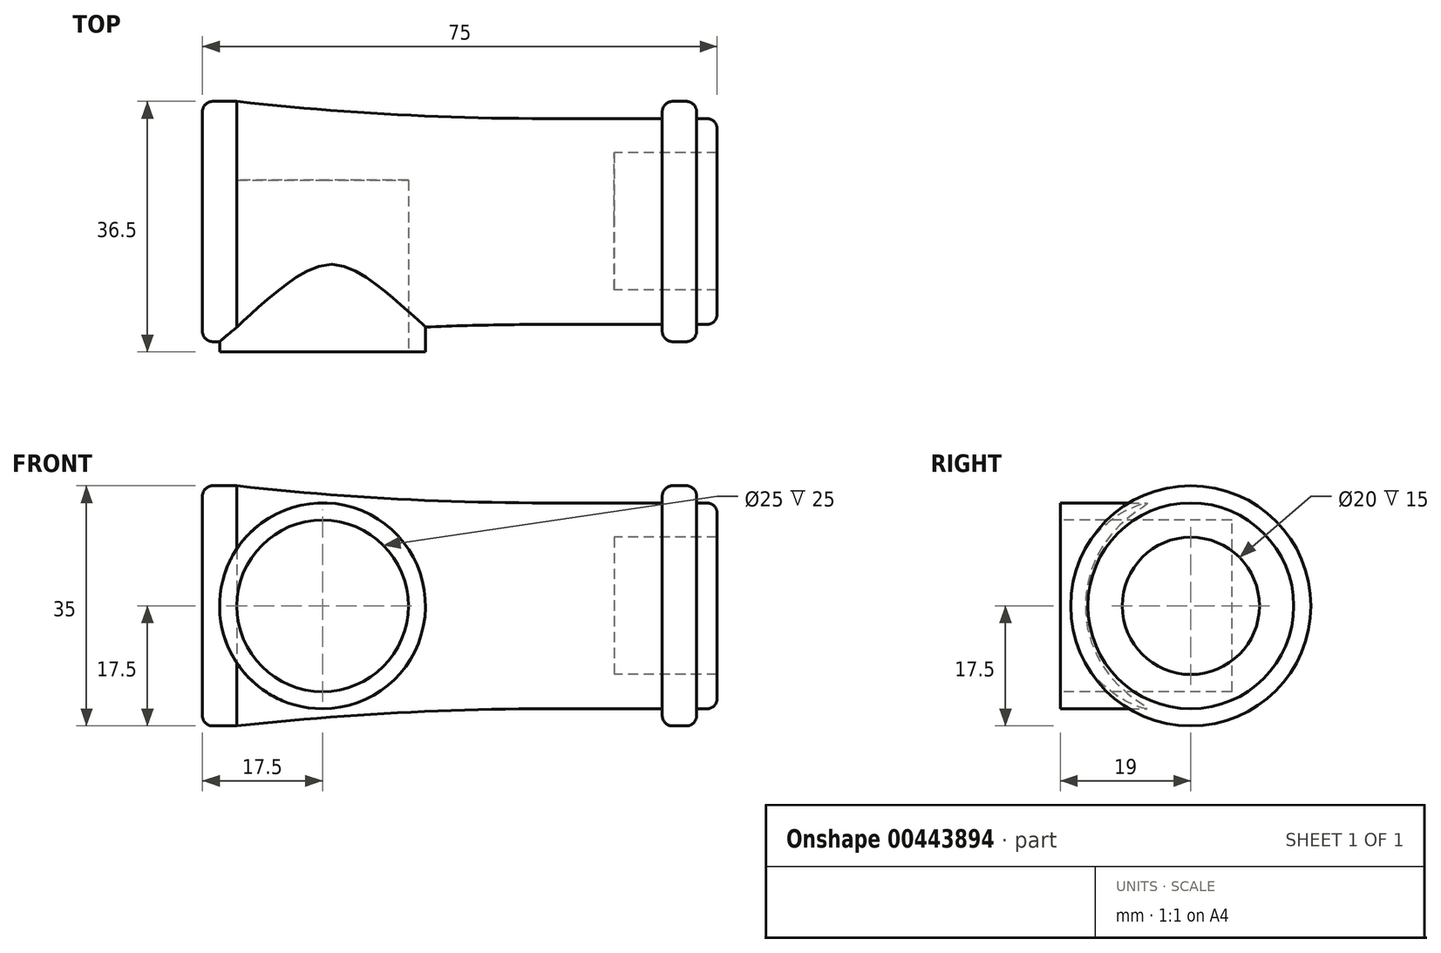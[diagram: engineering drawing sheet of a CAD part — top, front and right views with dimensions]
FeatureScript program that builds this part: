
annotation { "Feature Type Name" : "Feature", "Feature Type Description" : "" }
export const myFeature = defineFeature(function(context is Context, id is Id, definition is map)
    precondition{}
    {
        {
            var Q0;
            Q0=qCreatedBy(makeId("Front.planeOp"),FACE);
            var sketch = newSketch(context, id + "F0", { "sketchPlane" : qUnion([Q0])});
            skLineSegment(sketch, "E0", {"start": v(0, 0) * mm, "end": v(0, 17.5) * mm});
            skLineSegment(sketch, "E1", {"start": v(0, 17.5) * mm, "end": v(5, 17.5) * mm});
            skLineSegment(sketch, "E2", {"start": v(0, 0) * mm, "end": v(60, 0) * mm});
            skLineSegment(sketch, "E3", {"start": v(60, 0) * mm, "end": v(60, 10) * mm});
            skLineSegment(sketch, "E4", {"start": v(60, 10) * mm, "end": v(75, 10) * mm});
            skLineSegment(sketch, "E5", {"start": v(75, 10) * mm, "end": v(75, 15) * mm});
            skLineSegment(sketch, "E6", {"start": v(75, 15) * mm, "end": v(72, 15) * mm});
            skLineSegment(sketch, "E7", {"start": v(72, 15) * mm, "end": v(72, 17.5) * mm});
            skLineSegment(sketch, "E8", {"start": v(72, 17.5) * mm, "end": v(67, 17.5) * mm});
            skLineSegment(sketch, "E9", {"start": v(67, 17.5) * mm, "end": v(67, 15) * mm});
            skLineSegment(sketch, "E10", {"start": v(67, 15) * mm, "end": v(50, 15) * mm});
            skArc(sketch, "E11", {"start": v(5, 17.5) * mm, "mid": v(27.47, 15.63) * mm, "end": v(50, 15) * mm});
            skSolve(sketch);
        }
        {
            var Q0;
            Q0 = qSketchRegion(id + "F0", true);
            var Q1;
            Q1=sQuery(id+"F0.wireOp",EDGE,"E2");
            revolve(context, id + "F1", {"entities" : qUnion([Q0]), "axis" : qUnion([Q1]), "revolveType" : RevolveType.FULL});
        }
        {
            var Q0;
            Q0=qCreatedBy(makeId("Front.planeOp"),FACE);
            var sketch = newSketch(context, id + "F2", { "sketchPlane" : qUnion([Q0])});
            skCircle(sketch, "E12", {"center": v(17.5, 0) * mm, "radius": 15 * mm});
            skSolve(sketch);
        }
        {
            var Q0;
            Q0 = qSketchRegion(id + "F2", true);
            extrude(context, id + "F3", {"entities" : qUnion([Q0]), "operationType" : NewBodyOperationType.ADD, "depth" : 19 * mm});
        }
        {
            var Q0;
            Q0=makeQuery(id+"F3.opExtrude","CAP_FACE",FACE,{"disambiguationData":[OSD([sQuery(id+"F2.wireOp",EDGE,"E12")])],"isStart":false});
            var sketch = newSketch(context, id + "F4", { "sketchPlane" : qUnion([Q0])});
            skCircle(sketch, "E13", {"center": v(17.5, 0) * mm, "radius": 12.5 * mm});
            skSolve(sketch);
        }
        {
            var Q0;
            Q0 = qSketchRegion(id + "F4", true);
            extrude(context, id + "F5", {"entities" : qUnion([Q0]), "operationType" : NewBodyOperationType.REMOVE, "oppositeDirection" : true, "depth" : 25 * mm});
        }
        {
            var Q0;
            Q0=makeQuery(id+"F1.opRevolve","SWEPT_FACE",FACE,{"disambiguationData":[OSD([sQuery(id+"F0.wireOp",EDGE,"E0")])]});
            var Q1;
            Q1=makeQuery(id+"F5.boolean.opBoolean","COPY",EDGE,{"derivedFrom":makeQuery(id+"F5.opExtrude","CAP_EDGE",EDGE,{"disambiguationData":[OSD([sQuery(id+"F4.wireOp",EDGE,"E13")])],"isStart":true})});
            var Q2;
            Q2=makeQuery(id+"F1.opRevolve","SWEPT_EDGE",EDGE,{"disambiguationData":[OSD([sQuery(id+"F0.wireOp",EDGE,"E5"),sQuery(id+"F0.wireOp",EDGE,"E6")])]});
            var Q3;
            Q3=makeQuery(id+"F1.opRevolve","SWEPT_EDGE",EDGE,{"disambiguationData":[OSD([sQuery(id+"F0.wireOp",EDGE,"E7"),sQuery(id+"F0.wireOp",EDGE,"E8")])]});
            var Q4;
            Q4=makeQuery(id+"F1.opRevolve","SWEPT_EDGE",EDGE,{"disambiguationData":[OSD([sQuery(id+"F0.wireOp",EDGE,"E8"),sQuery(id+"F0.wireOp",EDGE,"E9")])]});
            fillet(context, id + "F6", {"entities" : qUnion([Q0, Q1, Q2, Q3, Q4]), "radius" : 1.5 * mm, "tangentPropagation" : true, "allowEdgeOverflow" : false});
        }
    });
